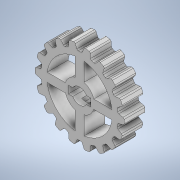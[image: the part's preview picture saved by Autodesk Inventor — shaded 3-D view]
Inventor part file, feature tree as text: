
AUTODESK INVENTOR PART (.ipt)
format: ipt  version: 2022 (Build 260153000, 153)  size: 467,456 bytes
history: native  units: mm
features: extrude x4, sketch x4, other x4, reference x2, plane x1, projected_geometry x1
ambient origin geometry x8: Origin, YZ Plane, XZ Plane, XY Plane, X Axis, Y Axis, Z Axis, Center Point
bodies: Solid1 (feature_tree)
feature tree (16):
  extrude  "Extrusion1"  Depth=10.0mm
  sketch  "Sketch2"  dims[d2=2.0mm d3=5.0mm d4=0.0mm d5=0.0mm d6=40.0mm d8=360.0deg]
  plane  "Work Plane1"
  extrude  "Extrusion2"  Depth=5.0mm TaperAngle=360.0deg
  extrude  "Extrusion3"  TaperAngle=0.0deg  [1 undecoded]
  extrude  "Extrusion4"  Depth=10.0mm
  sketch  "Sketch1"  dims[d0=10.0mm d1=0.3mm]
  reference  "Reference1"
  projected_geometry  "Projected Loop1"
  sketch  "Sketch3"  dims[d10=2.0mm d11=0.0mm d12=0.0mm d13=0.0mm]
  sketch  "Sketch4"  dims[d14=33.0mm d15=30.0mm d16=2.0mm d17=2.0mm d18=3.0mm d19=40.0mm d21=360.0deg d23=2.0mm d24=3.0mm d25=0.5mm d26=0.5mm d27=180.0mm d29=360.0deg d31=10.0mm d32=0.0mm]
  reference  "Reference2"
  other  "<userpath>\OneDrive - Imperial College London\ROBOICP\new vial holder assembly.iam"
  other  "new vial holder assembly.iam"
  other  "Mixer:1"
  other  "mixer_gear:5"
note: 1 required parameter value undecoded (feature->parameter linkage not recoverable at this tier; creation-order binding heuristic only, values carry confidence <= 0.55)
